FCSTD DOCUMENT  (FreeCAD 0.21R33694 (Git))
Label: OJT1_T18P01_restriccions
License: All rights reserved
LicenseURL: https://en.wikipedia.org/wiki/All_rights_reserved
objects: Sketcher::SketchObject×1, PartDesign::Body×1
note: 2 computed .brp shape members not serialized (recipe doc carries the construction recipe); baked Part::Feature solids carry a one-line shape summary decoded from their .brp

FEATURE [Sketcher::SketchObject] Sketch
  FullyConstrained = false
  MapMode = 5
  Support = -> [XY_Plane]
  sketch-geometry (58):
    g0: LineSegment StartX=-34.1493 StartY=0.908781 StartZ=0 EndX=25.8507 EndY=0.908781 EndZ=0
    g1: LineSegment StartX=27.3869 StartY=1.01579 StartZ=0 EndX=27.3869 EndY=-18.9842 EndZ=0
    g2: LineSegment StartX=-34.6078 StartY=-18.9842 StartZ=0 EndX=25.3922 EndY=-18.9842 EndZ=0
    g3: LineSegment StartX=-35.0685 StartY=0.908781 StartZ=0 EndX=-35.0685 EndY=-19.0912 EndZ=0
    g4: GeomPoint X=25.8507 Y=0.908781 Z=0
    g5: GeomPoint X=27.3869 Y=1.01579 Z=0
    g6: GeomPoint X=27.3869 Y=1.01579 Z=0
    g7: GeomPoint X=25.8507 Y=0.908781 Z=0
    g8: GeomPoint X=25.8507 Y=0.908781 Z=0
    g9: GeomPoint X=27.3869 Y=1.01579 Z=0
    g10: GeomPoint X=37.9397 Y=37.4372 Z=0
    g11: GeomPoint X=37.9397 Y=37.4372 Z=0
    g12: GeomPoint X=25.3922 Y=-18.9842 Z=0
    g13: GeomPoint X=27.3869 Y=-18.9842 Z=0
    g14: GeomPoint X=27.3869 Y=-18.9842 Z=0
    g15: GeomPoint X=-34.6078 Y=-18.9842 Z=0
    g16: GeomPoint X=-35.0685 Y=0.908781 Z=0
    g17: GeomPoint X=27.3869 Y=1.01579 Z=0
    g18: GeomPoint X=25.8507 Y=0.908781 Z=0
    g19: GeomPoint X=27.3869 Y=1.01579 Z=0
    g20: GeomPoint X=-34.6078 Y=-18.9842 Z=0
    g21: GeomPoint X=27.3869 Y=-18.9842 Z=0
    g22: GeomPoint X=25.8507 Y=0.908781 Z=0
    g23: GeomPoint X=0 Y=0 Z=0
    g24: GeomPoint X=0 Y=0 Z=0
    g25: GeomPoint X=0 Y=0 Z=0
    g26: GeomPoint X=0 Y=0 Z=0
    g27: GeomPoint X=27.3869 Y=-18.9842 Z=0
    g28: GeomPoint X=0 Y=0 Z=0
    g29: GeomPoint X=0 Y=0 Z=0
    g30: GeomPoint X=-35.0685 Y=-19.0912 Z=0
    g31: GeomPoint X=-35.0685 Y=-19.0912 Z=0
    g32: GeomPoint X=-35.0685 Y=0.908781 Z=0
    g33: GeomPoint X=-34.1493 Y=0.908781 Z=0
    g34: GeomPoint X=27.3869 Y=1.01579 Z=0
    g35: GeomPoint X=-35.0685 Y=-19.0912 Z=0
    g36: GeomPoint X=-35.0685 Y=0.908781 Z=0
    g37: GeomPoint X=-35.0685 Y=-19.0912 Z=0
    g38: GeomPoint X=27.3869 Y=1.7229 Z=0
    g39: GeomPoint X=27.3869 Y=1.01579 Z=0
    g40: GeomPoint X=27.3869 Y=1.01579 Z=0
    g41: GeomPoint X=-35.0685 Y=-21.1055 Z=0
    g42: GeomPoint X=-35.0685 Y=-21.1055 Z=0
    g43: GeomPoint X=0 Y=0 Z=0
    g44: GeomPoint X=-35.0685 Y=-19.0912 Z=0
    g45: GeomPoint X=0 Y=0 Z=0
    g46: GeomPoint X=0 Y=0 Z=0
    g47: GeomPoint X=-35.0685 Y=-21.1055 Z=0
    g48: GeomPoint X=-35.0685 Y=-19.0912 Z=0
    g49: GeomPoint X=0 Y=0 Z=0
    g50: GeomPoint X=25.3922 Y=-18.9842 Z=0
    g51: GeomPoint X=25.8507 Y=0.908781 Z=0
    g52: GeomPoint X=-34.6078 Y=-18.9842 Z=0
    g53: GeomPoint X=25.3922 Y=-18.9842 Z=0
    g54: GeomPoint X=-35.0685 Y=-19.0912 Z=0
    g55: GeomPoint X=-35.0685 Y=0.908781 Z=0
    g56: GeomPoint X=25.8507 Y=0.908781 Z=0
    g57: GeomPoint X=-34.1493 Y=0.908781 Z=0
  constraints (59):
    c: Coincident(g4,g0)
    c: Coincident(g5,g1)
    c: Coincident(g6,g1)
    c: Coincident(g7,g0)
    c: Coincident(g8,g0)
    c: Coincident(g9,g1)
    c: Coincident(g12,g2)
    c: Coincident(g13,g1)
    c: Coincident(g14,g1)
    c: Coincident(g15,g2)
    c: Coincident(g16,g3)
    c: Horizontal(g0)
    c: Coincident(g17,g1)
    c: Coincident(g18,g0)
    c: Coincident(g19,g1)
    c: Horizontal(g2)
    c: Vertical(g1)
    c: Vertical(g3)
    c: Coincident(g20,g2)
    c: Coincident(g21,g1)
    c: Coincident(g22,g0)
    c: Coincident(g23,g-1)
    c: Coincident(g24,g23)
    c: Coincident(g25,g23)
    c: Coincident(g26,g23)
    c: Coincident(g27,g1)
    c: Coincident(g28,g23)
    c: Coincident(g29,g23)
    c: DistanceY(g3,g3) = 20
    c: Coincident(g30,g3)
    c: Coincident(g31,g3)
    c: Coincident(g32,g3)
    c: Coincident(g33,g0)
    c: Coincident(g34,g1)
    c: Coincident(g35,g3)
    c: Coincident(g36,g3)
    c: Coincident(g37,g3)
    c: DistanceY(g1,g1) = 20
    c: PointOnObject(g38,g1)
    c: Coincident(g39,g1)
    c: Coincident(g40,g1)
    c: DistanceX(g0,g0) = 60
    c: DistanceX(g2,g2) = 60
    c: PointOnObject(g41,g3)
    c: PointOnObject(g42,g3)
    c: Coincident(g43,g23)
    c: Coincident(g44,g3)
    c: Coincident(g45,g23)
    c: Coincident(g47,g41)
    c: Coincident(g48,g3)
    c: Coincident(g49,g23)
    c: Coincident(g50,g2)
    c: Coincident(g51,g0)
    c: Coincident(g52,g2)
    c: Coincident(g53,g2)
    c: Coincident(g54,g3)
    c: Coincident(g55,g3)
    c: Coincident(g56,g0)
    c: Coincident(g57,g0)
FEATURE [PartDesign::Body] Body  label="RESTRICCIONS-PRACTICA1"
  Group = -> [Sketch]
  Origin = -> Origin
